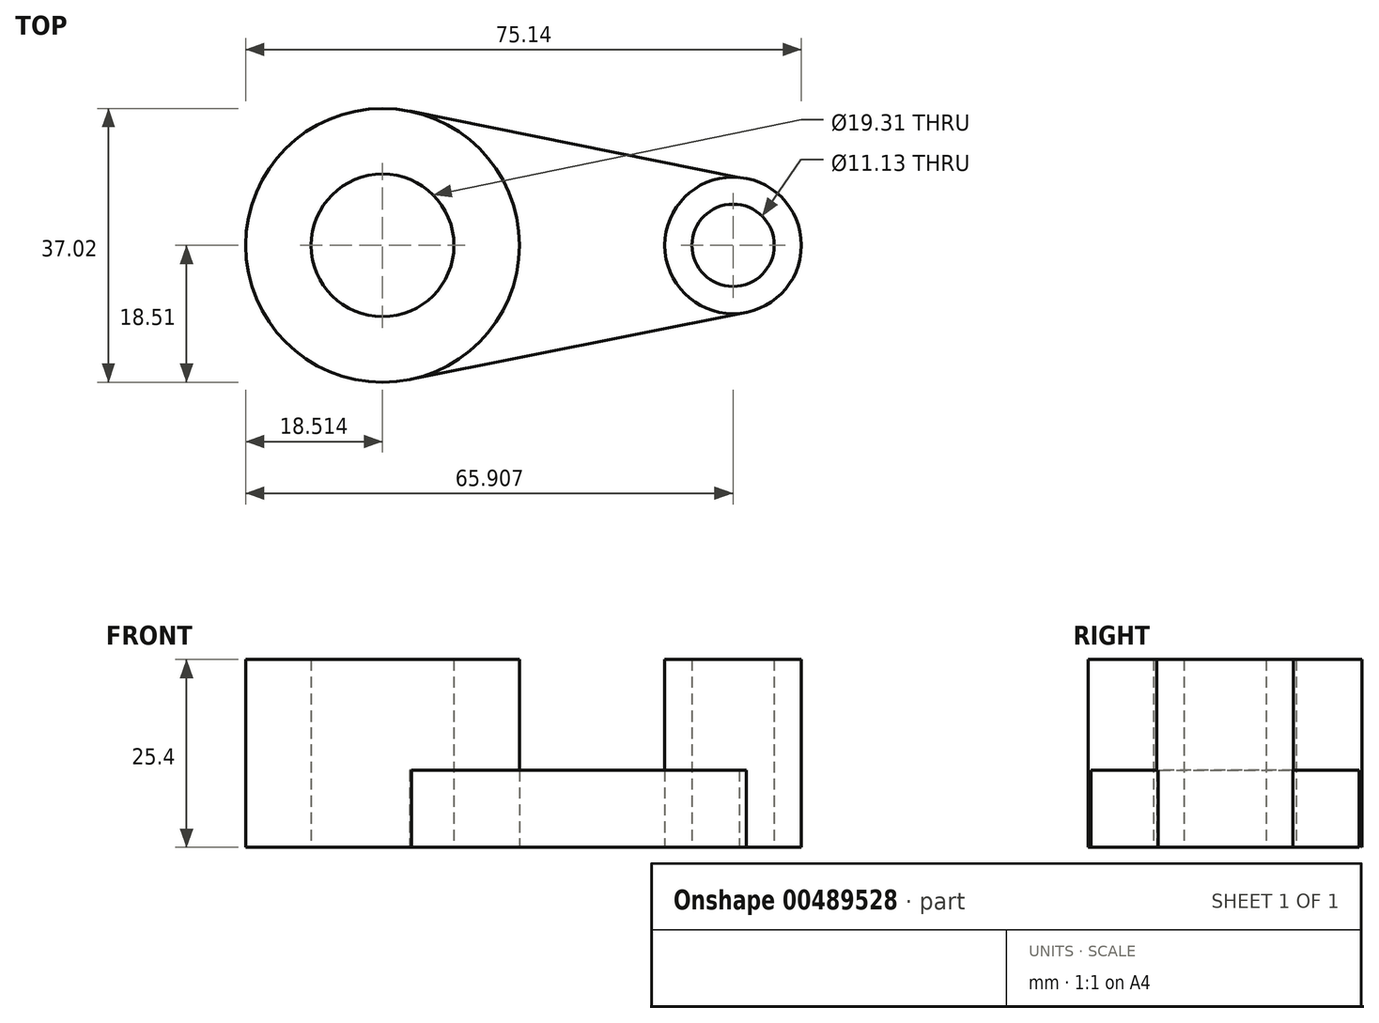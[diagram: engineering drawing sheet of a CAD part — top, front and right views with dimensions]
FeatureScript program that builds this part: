
annotation { "Feature Type Name" : "Feature", "Feature Type Description" : "" }
export const myFeature = defineFeature(function(context is Context, id is Id, definition is map)
    precondition{}
    {
        {
            var Q0;
            Q0=qCreatedBy(makeId("Top.planeOp"),FACE);
            var sketch = newSketch(context, id + "F0", { "sketchPlane" : qUnion([Q0])});
            skCircle(sketch, "E0", {"center": v(-23.84, 0) * mm, "radius": 18.51 * mm});
            skCircle(sketch, "E1", {"center": v(23.56, 0) * mm, "radius": 9.23 * mm});
            skSolve(sketch);
        }
        {
            var Q0;
            Q0=makeQuery(id+"F0.imprint","IMPRINT",FACE,{"disambiguationData":[TD([[makeQuery(id+"F0.imprint","IMPRINT",EDGE,{"derivedFrom":sQuery(id+"F0.wireOp",EDGE,"E0")}),1.0]])]});
            var sketch = newSketch(context, id + "F1", { "sketchPlane" : qUnion([Q0])});
            skLineSegment(sketch, "E2", {"start": v(-20.5, -18.2) * mm, "end": v(25.36, -9.05) * mm});
            skLineSegment(sketch, "E3", {"start": v(-20.19, 18.15) * mm, "end": v(24.4, 9.2) * mm});
            skArc(sketch, "E4", {"start": v(24.4, 9.2) * mm, "mid": v(14.34, -0.49) * mm, "end": v(25.36, -9.05) * mm});
            skSolve(sketch);
        }
        {
            var Q0;
            Q0=makeQuery(id+"F0.imprint","IMPRINT",FACE,{"disambiguationData":[TD([[makeQuery(id+"F0.imprint","IMPRINT",EDGE,{"derivedFrom":sQuery(id+"F0.wireOp",EDGE,"E0")}),1.0]])]});
            var sketch = newSketch(context, id + "F2", { "sketchPlane" : qUnion([Q0])});
            skCircle(sketch, "E5", {"center": v(-23.84, 0) * mm, "radius": 9.65 * mm});
            skCircle(sketch, "E6", {"center": v(23.56, 0) * mm, "radius": 5.57 * mm});
            skSolve(sketch);
        }
        {
            var Q0;
            Q0=makeQuery(id+"F0.imprint","IMPRINT",FACE,{"disambiguationData":[TD([[makeQuery(id+"F0.imprint","IMPRINT",EDGE,{"derivedFrom":sQuery(id+"F0.wireOp",EDGE,"E0")}),1.0]])]});
            var Q1;
            Q1=makeQuery(id+"F0.imprint","IMPRINT",FACE,{"disambiguationData":[TD([[makeQuery(id+"F0.imprint","IMPRINT",EDGE,{"derivedFrom":sQuery(id+"F0.wireOp",EDGE,"E1")}),1.0]])]});
            extrude(context, id + "F3", {"entities" : qUnion([Q0, Q1]), "depth" : 25.4 * mm, "offsetDistance" : 25.4 * mm});
        }
        {
            var Q0;
            Q0=makeQuery(id+"F2.imprint","IMPRINT",FACE,{"disambiguationData":[TD([[makeQuery(id+"F2.imprint","IMPRINT",EDGE,{"derivedFrom":sQuery(id+"F2.wireOp",EDGE,"E6")}),1.0]])]});
            var Q1;
            Q1=makeQuery(id+"F2.imprint","IMPRINT",FACE,{"disambiguationData":[TD([[makeQuery(id+"F2.imprint","IMPRINT",EDGE,{"derivedFrom":sQuery(id+"F2.wireOp",EDGE,"E5")}),1.0]])]});
            extrude(context, id + "F4", {"entities" : qUnion([Q0, Q1]), "operationType" : NewBodyOperationType.REMOVE, "depth" : 228.6 * mm, "offsetDistance" : 25.4 * mm});
        }
        {
            var Q0;
            {var subQ4=sQuery(id+"F1.wireOp",EDGE,"E3");Q0=makeQuery(id+"F1.imprint","IMPRINT",FACE,{"disambiguationData":[TD([[makeQuery(id+"F1.imprint","IMPRINT",EDGE,{"derivedFrom":subQ4}),-1.0]])]});}
            extrude(context, id + "F5", {"entities" : qUnion([Q0]), "depth" : 10.4 * mm, "offsetDistance" : 25.4 * mm});
        }
    });
